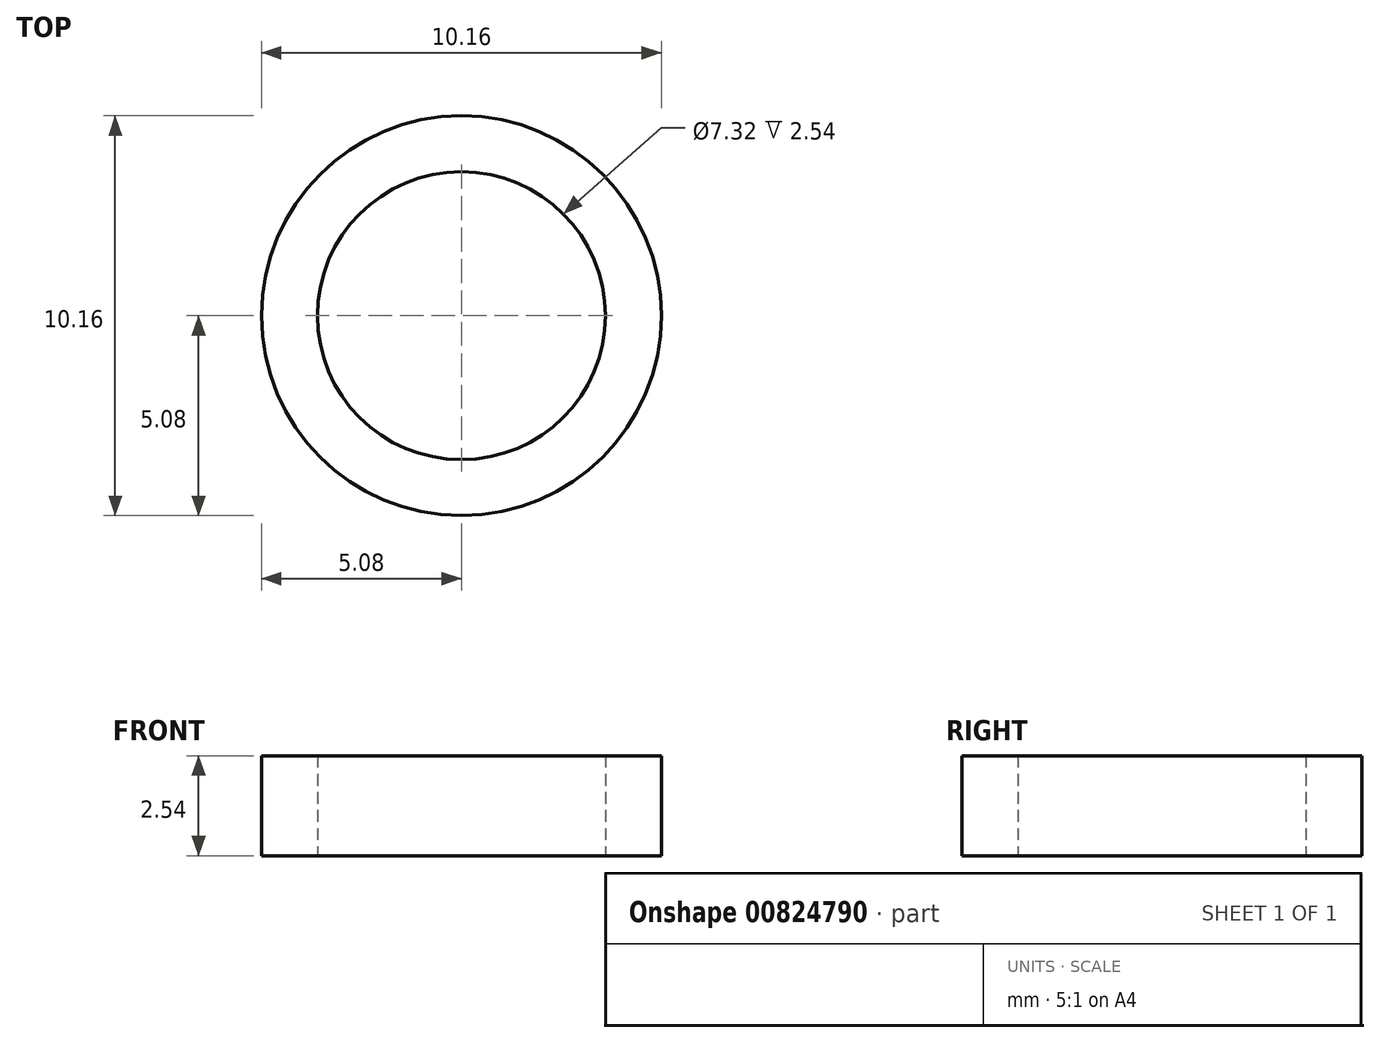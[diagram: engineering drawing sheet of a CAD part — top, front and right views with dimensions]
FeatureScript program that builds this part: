
annotation { "Feature Type Name" : "Feature", "Feature Type Description" : "" }
export const myFeature = defineFeature(function(context is Context, id is Id, definition is map)
    precondition{}
    {
        {
            var Q0;
            Q0=qCreatedBy(makeId("Top.planeOp"),FACE);
            var sketch = newSketch(context, id + "F0", { "sketchPlane" : qUnion([Q0])});
            skCircle(sketch, "E0", {"center": v(0, 0) * mm, "radius": 3.66 * mm});
            skCircle(sketch, "E1", {"center": v(0, 0) * mm, "radius": 5.08 * mm});
            skLineSegment(sketch, "E2", {"start": v(0, 0) * mm, "end": v(3.66, 0) * mm, "construction": true});
            skSolve(sketch);
        }
        {
            var Q0;
            Q0=makeQuery(id+"F0.imprint","IMPRINT",FACE,{"disambiguationData":[TD([[makeQuery(id+"F0.imprint","IMPRINT",EDGE,{"derivedFrom":sQuery(id+"F0.wireOp",EDGE,"E0")}),-1.0]])]});
            extrude(context, id + "F1", {"entities" : qUnion([Q0]), "depth" : 2.54 * mm, "offsetDistance" : 25.4 * mm});
        }
    });
